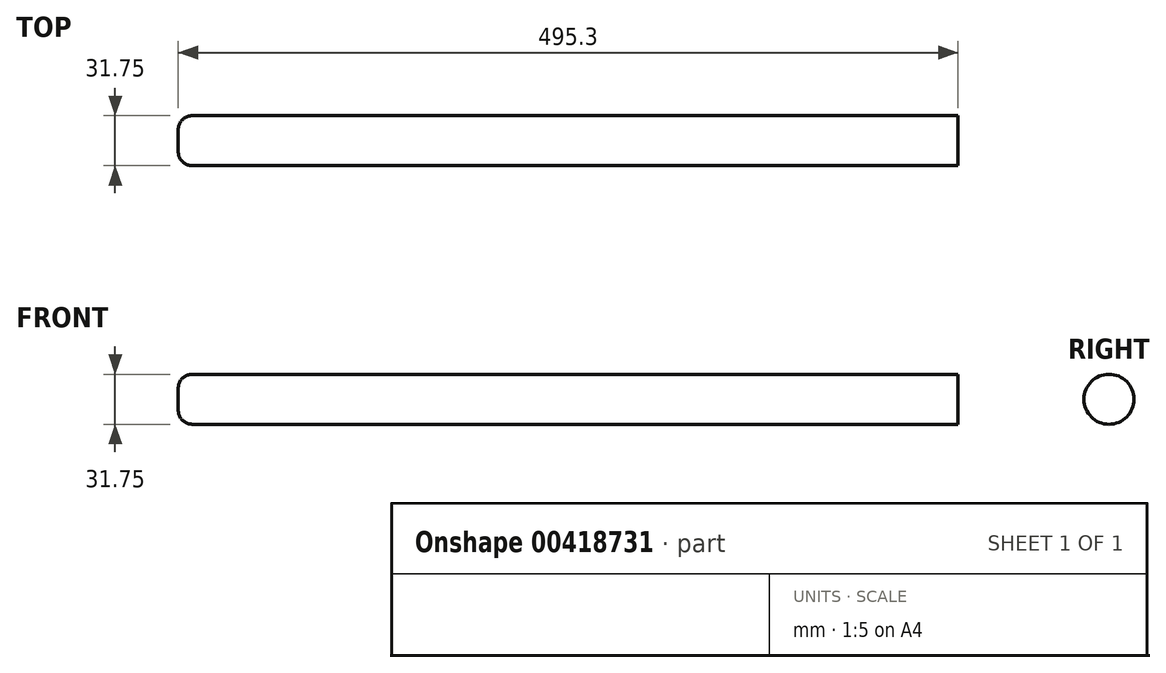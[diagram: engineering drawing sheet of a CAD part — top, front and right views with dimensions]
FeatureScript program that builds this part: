
annotation { "Feature Type Name" : "Feature", "Feature Type Description" : "" }
export const myFeature = defineFeature(function(context is Context, id is Id, definition is map)
    precondition{}
    {
        {
            var Q0;
            Q0=qCreatedBy(makeId("Right.planeOp"),FACE);
            var sketch = newSketch(context, id + "F0", { "sketchPlane" : qUnion([Q0])});
            skCircle(sketch, "E0.0", {"center": v(-180.08, 19.4) * mm, "radius": 15.88 * mm});
            skSolve(sketch);
        }
        {
            var Q0;
            Q0=makeQuery(id+"F0.imprint","IMPRINT",FACE,{"disambiguationData":[TD([[makeQuery(id+"F0.imprint","IMPRINT",EDGE,{"derivedFrom":sQuery(id+"F0.wireOp",EDGE,"E0.0")}),1.0]])]});
            extrude(context, id + "F1", {"entities" : qUnion([Q0]), "depth" : 495.3 * mm});
        }
        {
            var Q0;
            Q0=makeQuery(id+"F1.opExtrude","CAP_EDGE",EDGE,{"disambiguationData":[OSD([sQuery(id+"F0.wireOp",EDGE,"E0.0")])],"isStart":true});
            fillet(context, id + "F2", {"entities" : qUnion([Q0]), "radius" : 8.9 * mm, "tangentPropagation" : true, "allowEdgeOverflow" : false});
        }
    });
